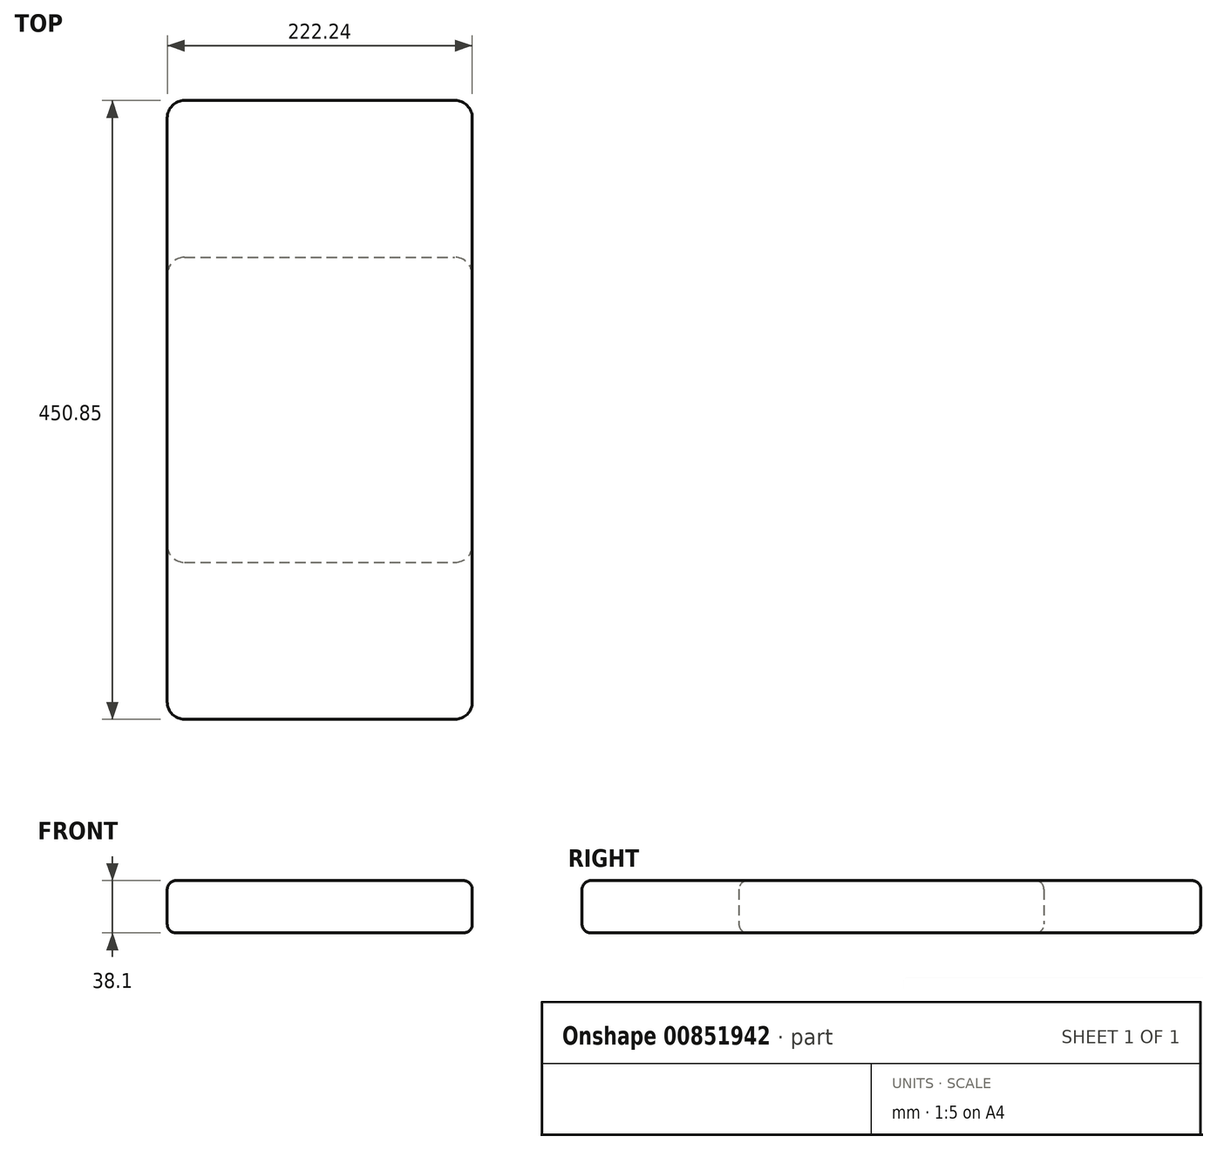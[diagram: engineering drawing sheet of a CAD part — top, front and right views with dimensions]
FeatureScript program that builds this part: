
annotation { "Feature Type Name" : "Feature", "Feature Type Description" : "" }
export const myFeature = defineFeature(function(context is Context, id is Id, definition is map)
    precondition{}
    {
        {
            var Q0;
            Q0=qCreatedBy(makeId("Top.planeOp"),FACE);
            var sketch = newSketch(context, id + "F0", { "sketchPlane" : qUnion([Q0])});
            skLineSegment(sketch, "E0.bottom", {"start": v(-111.13, 111.13) * mm, "end": v(111.13, 111.12) * mm});
            skLineSegment(sketch, "E0.top", {"start": v(-111.13, -111.12) * mm, "end": v(111.12, -111.13) * mm});
            skLineSegment(sketch, "E0.left", {"start": v(-111.12, 111.12) * mm, "end": v(-111.13, -111.12) * mm});
            skLineSegment(sketch, "E0.right", {"start": v(111.13, 111.12) * mm, "end": v(111.12, -111.12) * mm});
            skSolve(sketch);
        }
        {
            var Q0;
            Q0=qCreatedBy(makeId("Top.planeOp"),FACE);
            var sketch = newSketch(context, id + "F1", { "sketchPlane" : qUnion([Q0])});
            skLineSegment(sketch, "E1.bottom", {"start": v(-111.13, 225.43) * mm, "end": v(111.13, 225.42) * mm});
            skLineSegment(sketch, "E1.top", {"start": v(-111.13, -225.42) * mm, "end": v(111.13, -225.43) * mm});
            skLineSegment(sketch, "E1.left", {"start": v(-111.12, 225.42) * mm, "end": v(-111.13, -225.42) * mm});
            skLineSegment(sketch, "E1.right", {"start": v(111.13, 225.42) * mm, "end": v(111.12, -225.42) * mm});
            skSolve(sketch);
        }
        {
            var Q0;
            Q0 = qSketchRegion(id + "F0", true);
            extrude(context, id + "F2", {"entities" : qUnion([Q0]), "depth" : 38.1 * mm, "offsetDistance" : 30.48 * mm});
        }
        {
            var Q0;
            Q0=makeQuery(id+"F2.opExtrude","SWEPT_EDGE",EDGE,{"disambiguationData":[OSD([sQuery(id+"F0.wireOp",EDGE,"E0.top"),sQuery(id+"F0.wireOp",EDGE,"E0.left")])]});
            var Q1;
            Q1=makeQuery(id+"F2.opExtrude","SWEPT_EDGE",EDGE,{"disambiguationData":[OSD([sQuery(id+"F0.wireOp",EDGE,"E0.top"),sQuery(id+"F0.wireOp",EDGE,"E0.right")])]});
            var Q2;
            Q2=makeQuery(id+"F2.opExtrude","SWEPT_EDGE",EDGE,{"disambiguationData":[OSD([sQuery(id+"F0.wireOp",EDGE,"E0.bottom"),sQuery(id+"F0.wireOp",EDGE,"E0.right")])]});
            var Q3;
            Q3=makeQuery(id+"F2.opExtrude","SWEPT_EDGE",EDGE,{"disambiguationData":[OSD([sQuery(id+"F0.wireOp",EDGE,"E0.bottom"),sQuery(id+"F0.wireOp",EDGE,"E0.left")])]});
            fillet(context, id + "F3", {"entities" : qUnion([Q0, Q1, Q2, Q3]), "radius" : 12.7 * mm, "tangentPropagation" : true, "allowEdgeOverflow" : false});
        }
        {
            var Q0;
            Q0=makeQuery(id+"F2.opExtrude","CAP_FACE",FACE,{"disambiguationData":[OSD([sQuery(id+"F0.wireOp",EDGE,"E0.bottom"),sQuery(id+"F0.wireOp",EDGE,"E0.top"),sQuery(id+"F0.wireOp",EDGE,"E0.left"),sQuery(id+"F0.wireOp",EDGE,"E0.right")])],"isStart":false});
            var Q1;
            Q1=makeQuery(id+"F2.opExtrude","CAP_FACE",FACE,{"disambiguationData":[OSD([sQuery(id+"F0.wireOp",EDGE,"E0.bottom"),sQuery(id+"F0.wireOp",EDGE,"E0.top"),sQuery(id+"F0.wireOp",EDGE,"E0.left"),sQuery(id+"F0.wireOp",EDGE,"E0.right")])],"isStart":true});
            fillet(context, id + "F4", {"entities" : qUnion([Q0, Q1]), "radius" : 6.35 * mm, "tangentPropagation" : true, "allowEdgeOverflow" : false});
        }
        {
            var Q0;
            Q0 = qSketchRegion(id + "F1", true);
            extrude(context, id + "F5", {"entities" : qUnion([Q0]), "depth" : 38.1 * mm, "offsetDistance" : 30.48 * mm});
        }
        {
            var Q0;
            Q0=makeQuery(id+"F5.opExtrude","SWEPT_EDGE",EDGE,{"disambiguationData":[OSD([sQuery(id+"F1.wireOp",EDGE,"E1.top"),sQuery(id+"F1.wireOp",EDGE,"E1.left")])]});
            var Q1;
            Q1=makeQuery(id+"F5.opExtrude","SWEPT_EDGE",EDGE,{"disambiguationData":[OSD([sQuery(id+"F1.wireOp",EDGE,"E1.top"),sQuery(id+"F1.wireOp",EDGE,"E1.right")])]});
            var Q2;
            Q2=makeQuery(id+"F5.opExtrude","SWEPT_EDGE",EDGE,{"disambiguationData":[OSD([sQuery(id+"F1.wireOp",EDGE,"E1.bottom"),sQuery(id+"F1.wireOp",EDGE,"E1.right")])]});
            var Q3;
            Q3=makeQuery(id+"F5.opExtrude","SWEPT_EDGE",EDGE,{"disambiguationData":[OSD([sQuery(id+"F1.wireOp",EDGE,"E1.bottom"),sQuery(id+"F1.wireOp",EDGE,"E1.left")])]});
            fillet(context, id + "F6", {"entities" : qUnion([Q0, Q1, Q2, Q3]), "radius" : 12.7 * mm, "tangentPropagation" : true, "allowEdgeOverflow" : false});
        }
        {
            var Q0;
            Q0=makeQuery(id+"F5.opExtrude","CAP_FACE",FACE,{"disambiguationData":[OSD([sQuery(id+"F1.wireOp",EDGE,"E1.bottom"),sQuery(id+"F1.wireOp",EDGE,"E1.top"),sQuery(id+"F1.wireOp",EDGE,"E1.left"),sQuery(id+"F1.wireOp",EDGE,"E1.right")])],"isStart":false});
            var Q1;
            Q1=makeQuery(id+"F5.opExtrude","CAP_FACE",FACE,{"disambiguationData":[OSD([sQuery(id+"F1.wireOp",EDGE,"E1.bottom"),sQuery(id+"F1.wireOp",EDGE,"E1.top"),sQuery(id+"F1.wireOp",EDGE,"E1.left"),sQuery(id+"F1.wireOp",EDGE,"E1.right")])],"isStart":true});
            fillet(context, id + "F7", {"entities" : qUnion([Q0, Q1]), "radius" : 6.35 * mm, "tangentPropagation" : true, "allowEdgeOverflow" : false});
        }
    });
